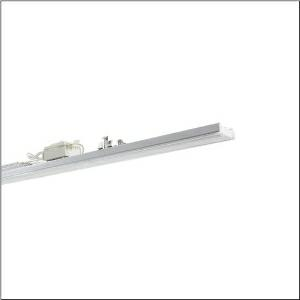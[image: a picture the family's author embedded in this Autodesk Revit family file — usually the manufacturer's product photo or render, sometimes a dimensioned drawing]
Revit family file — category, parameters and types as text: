
# Revit family: licross_r__11_recessed_mo_51te18dv4e5g_e61a
name_source: partatom
category: Lighting Fixtures
units: mm (PartAtom-declared; Revit-internal decimal feet)

## family parameters
Cut with Voids When Loaded = No
Host = Face
Light Source = No
Part Type = Normal
Room Calculation Point = No
Round Connector Dimension = Use Diameter
Shared = No

## types (1)
- --- (1 x LED, 14920 lm, 84.1 W, 4000K)
    Apparent Load = 84 VA
    CIE Flux Codes = 83 96 99 100 100
    Color Rendering = 80
    Color Temperature = 4000K
    Default Elevation = 1800 mm
    Description = Licross® 11 Recessed MO, luminaire insert, of sheet steel, galvanised, coil coated, white, length: 2.250mm, width: 66mm, height: 67mm, LED rated luminous flux: 14.920lm, light colour: 840, control gear: DALI 2, with plug, 5-pole, with phase selection, mains connection: 220..240V, AC, 50/60Hz, rated input power: 84W, halogen-free wiring, primary light control with lens, of plastic, primary optical cover: cover, of PMMA, light emission: direct distribution, primary light characteristic: symmetric, protection rating (complete): IP54, insulation class (complete): insulation class I (protective earthing), certification: CE, ENEC, VDE, UKCA, protection symbol: D if used in an environment with non-conductive dust loads with corresponding accessories, impact resistance: IK06, permissible ambient temperature for indoor applications: -25..+35°C, corresponds to IFS (International Featured Standards) requirements for safety and quality in the food industry, reducing of maximum allowable ambient temperature of 5°C with ceiling mounting, LABS conformity tested according to VDMA 24364:2018-05, packaging unit: 1 piece
    Height = 58 mm
    Lamp = 1 x LED
    Lamp Light Flux = 14920 lm
    Lamp Power = 84.1 W
    Lamp count = 1
    Length = 2250 mm
    Luminous efficacy = 177 lm/W
    Manufacturer = Siteco
    ModVariant = No
    Model = 51TE18DV4E5G
    Mounting Place = Ceiling
    Mounting Type = Pendant
    Number of Poles = 1
    OnlyDefault = Yes
    Power Factor = 1
    Product Name = Licross® 11 Recessed MO
    Product group = luminaire insert
    ProductGroupID = 902
    Protection Class = Protection class I
    Protection Degree = IP 54
    RLX_Detail_Level = 1
    RLX_Emergency_Light_Flux = 0 lm
    RLX_Emergency_Type = 0
    RLX_Emergency_Type_DB = No
    RlxData = <blob elided: 29585 chars, md5=0fa57785>
    Socket = socket
    Standby Power = 0 W
    System Light Flux = 14920 lm
    System Power = 84 W
    Type Comments = factory setting: luminous flux: 100 % | dim-lin: 254 | 378 mA
    Type Image = l_1296930.jpg
    URL = http://relux.com
    VarID = @adj_099030
    Voltage = 0 V
    Weight = 0.00 kg
    Width = 66 mm

## geometry (parser evidence)
native form markers: Blend x4, Sweep x11
no freeform markers — native parametric forms only
